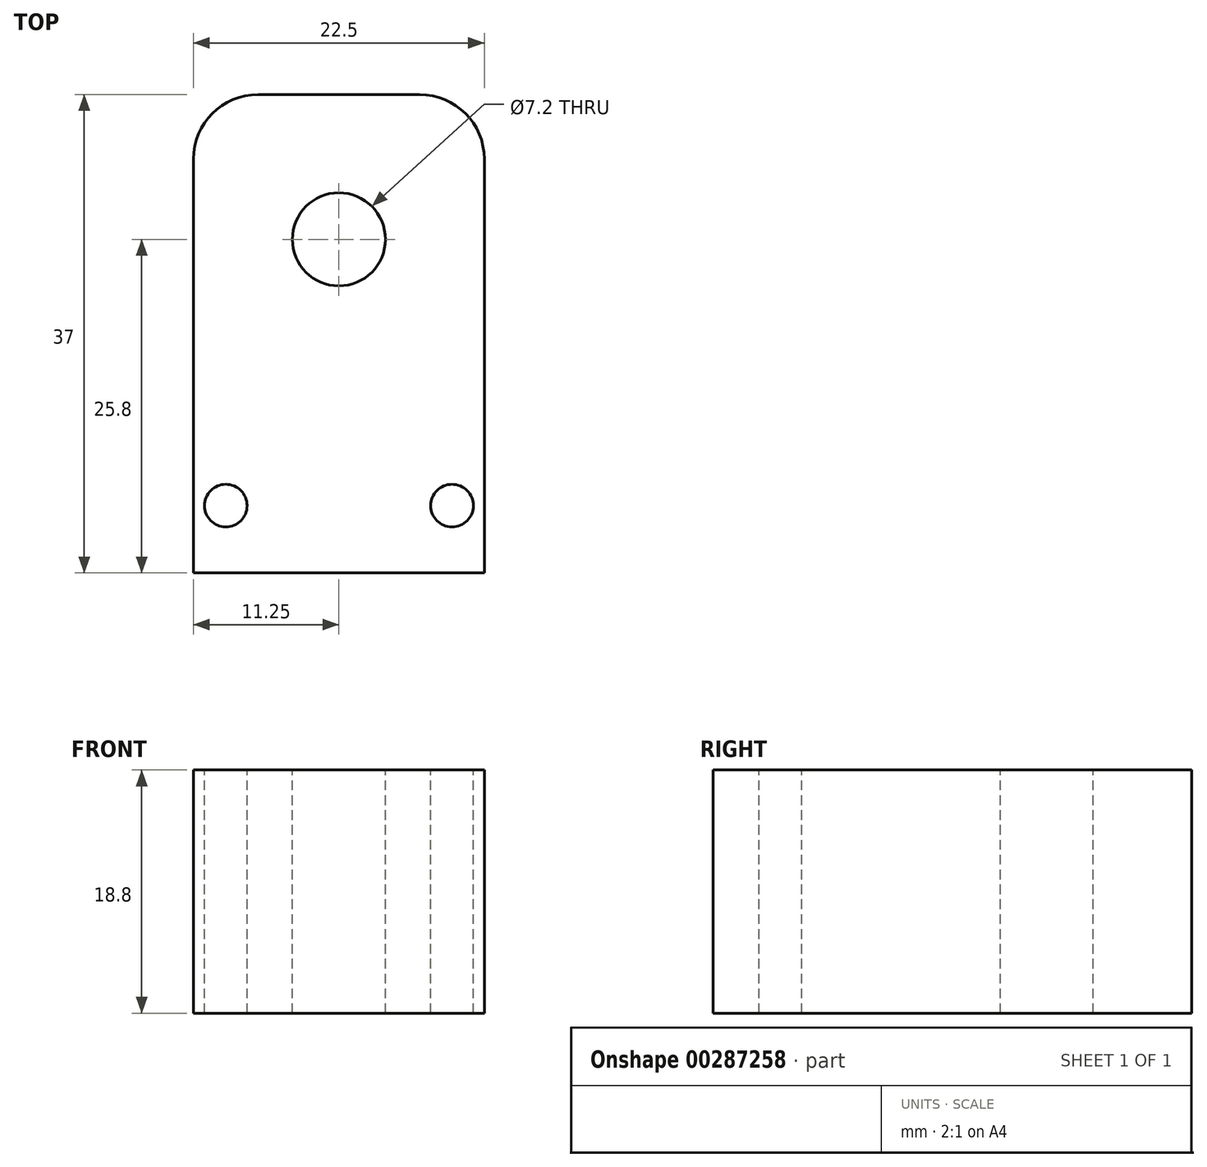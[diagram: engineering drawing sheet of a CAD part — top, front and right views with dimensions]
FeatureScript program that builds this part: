
annotation { "Feature Type Name" : "Feature", "Feature Type Description" : "" }
export const myFeature = defineFeature(function(context is Context, id is Id, definition is map)
    precondition{}
    {
        {
            var Q0;
            Q0=qCreatedBy(makeId("Top.planeOp"),FACE);
            var sketch = newSketch(context, id + "F0", { "sketchPlane" : qUnion([Q0])});
            skLineSegment(sketch, "E0.bottom", {"start": v(11.25, -18.5) * mm, "end": v(-11.25, -18.5) * mm});
            skLineSegment(sketch, "E0.top", {"start": v(11.25, 18.5) * mm, "end": v(-11.25, 18.5) * mm});
            skLineSegment(sketch, "E0.left", {"start": v(11.25, -18.5) * mm, "end": v(11.25, 18.5) * mm});
            skLineSegment(sketch, "E0.right", {"start": v(-11.25, -18.5) * mm, "end": v(-11.25, 18.5) * mm});
            skPoint(sketch, "E0.middle", {"position": v(0, 0) * mm});
            skSolve(sketch);
        }
        {
            var Q0;
            Q0=makeQuery(id+"F0.imprint","IMPRINT",FACE,{"disambiguationData":[TD([[makeQuery(id+"F0.imprint","IMPRINT",EDGE,{"derivedFrom":sQuery(id+"F0.wireOp",EDGE,"E0.bottom")}),-1.0]])]});
            extrude(context, id + "F1", {"entities" : qUnion([Q0]), "depth" : 18.8 * mm});
        }
        {
            var Q0;
            Q0=makeQuery(id+"F1.opExtrude","SWEPT_EDGE",EDGE,{"disambiguationData":[OSD([sQuery(id+"F0.wireOp",EDGE,"E0.top"),sQuery(id+"F0.wireOp",EDGE,"E0.left")])]});
            var Q1;
            Q1=makeQuery(id+"F1.opExtrude","SWEPT_EDGE",EDGE,{"disambiguationData":[OSD([sQuery(id+"F0.wireOp",EDGE,"E0.top"),sQuery(id+"F0.wireOp",EDGE,"E0.right")])]});
            fillet(context, id + "F2", {"entities" : qUnion([Q0, Q1]), "radius" : 5 * mm, "tangentPropagation" : true, "allowEdgeOverflow" : false});
        }
        {
            var Q0;
            Q0=makeQuery(id+"F1.opExtrude","CAP_FACE",FACE,{"disambiguationData":[OSD([sQuery(id+"F0.wireOp",EDGE,"E0.bottom"),sQuery(id+"F0.wireOp",EDGE,"E0.top"),sQuery(id+"F0.wireOp",EDGE,"E0.left"),sQuery(id+"F0.wireOp",EDGE,"E0.right")])],"isStart":false});
            var sketch = newSketch(context, id + "F3", { "sketchPlane" : qUnion([Q0])});
            skPoint(sketch, "E1.positionSnap0", {"position": v(0, 18.5) * mm});
            skPoint(sketch, "E2", {"position": v(-8.75, -13.3) * mm});
            skPoint(sketch, "E3.MirrorP", {"position": v(8.75, -13.3) * mm});
            skSolve(sketch);
        }
        {
            var Q0;
            Q0=sQuery(id+"F3.wireOp",VERTEX,"E2");
            var Q1;
            Q1=sQuery(id+"F3.wireOp",VERTEX,"E3.MirrorP");
            var Q2;
            Q2=makeQuery(id+"F1.opExtrude","SWEPT_BODY",BODY,{"disambiguationData":[OSD([sQuery(id+"F0.wireOp",EDGE,"E0.bottom"),sQuery(id+"F0.wireOp",EDGE,"E0.top"),sQuery(id+"F0.wireOp",EDGE,"E0.left"),sQuery(id+"F0.wireOp",EDGE,"E0.right")])]});
            hole(context, id + "F4", {"style" : HoleStyle.SIMPLE, "endStyle" : HoleEndStyle.THROUGH, "standardTappedOrClearance" : lookupTablePath({ "standard" : "ISO", "fit" : "Normal", "size" : "M3", "type" : "Clearance" }), "standardBlindInLast" : lookupTablePath({ "fit" : "Standard", "standard" : "ISO", "size" : "M3", "type" : "Clearance" }), "holeDiameter" : 3.3 * mm, "tappedDepth" : 12 * mm, "tapClearance" : 3, "locations" : qUnion([Q0, Q1]), "scope" : qUnion([Q2])});
        }
        {
            var Q0;
            Q0=makeQuery(id+"F1.opExtrude","CAP_FACE",FACE,{"disambiguationData":[OSD([sQuery(id+"F0.wireOp",EDGE,"E0.bottom"),sQuery(id+"F0.wireOp",EDGE,"E0.top"),sQuery(id+"F0.wireOp",EDGE,"E0.left"),sQuery(id+"F0.wireOp",EDGE,"E0.right")])],"isStart":false});
            var sketch = newSketch(context, id + "F5", { "sketchPlane" : qUnion([Q0])});
            skPoint(sketch, "E4", {"position": v(0, 7.3) * mm});
            skSolve(sketch);
        }
        {
            var Q0;
            Q0=sQuery(id+"F5.wireOp",VERTEX,"E4");
            var Q1;
            Q1=makeQuery(id+"F1.opExtrude","SWEPT_BODY",BODY,{"disambiguationData":[OSD([sQuery(id+"F0.wireOp",EDGE,"E0.bottom"),sQuery(id+"F0.wireOp",EDGE,"E0.top"),sQuery(id+"F0.wireOp",EDGE,"E0.left"),sQuery(id+"F0.wireOp",EDGE,"E0.right")])]});
            hole(context, id + "F6", {"style" : HoleStyle.SIMPLE, "endStyle" : HoleEndStyle.THROUGH, "holeDiameter" : 7.2 * mm, "tappedDepth" : 12 * mm, "tapClearance" : 3, "locations" : qUnion([Q0]), "scope" : qUnion([Q1])});
        }
    });
